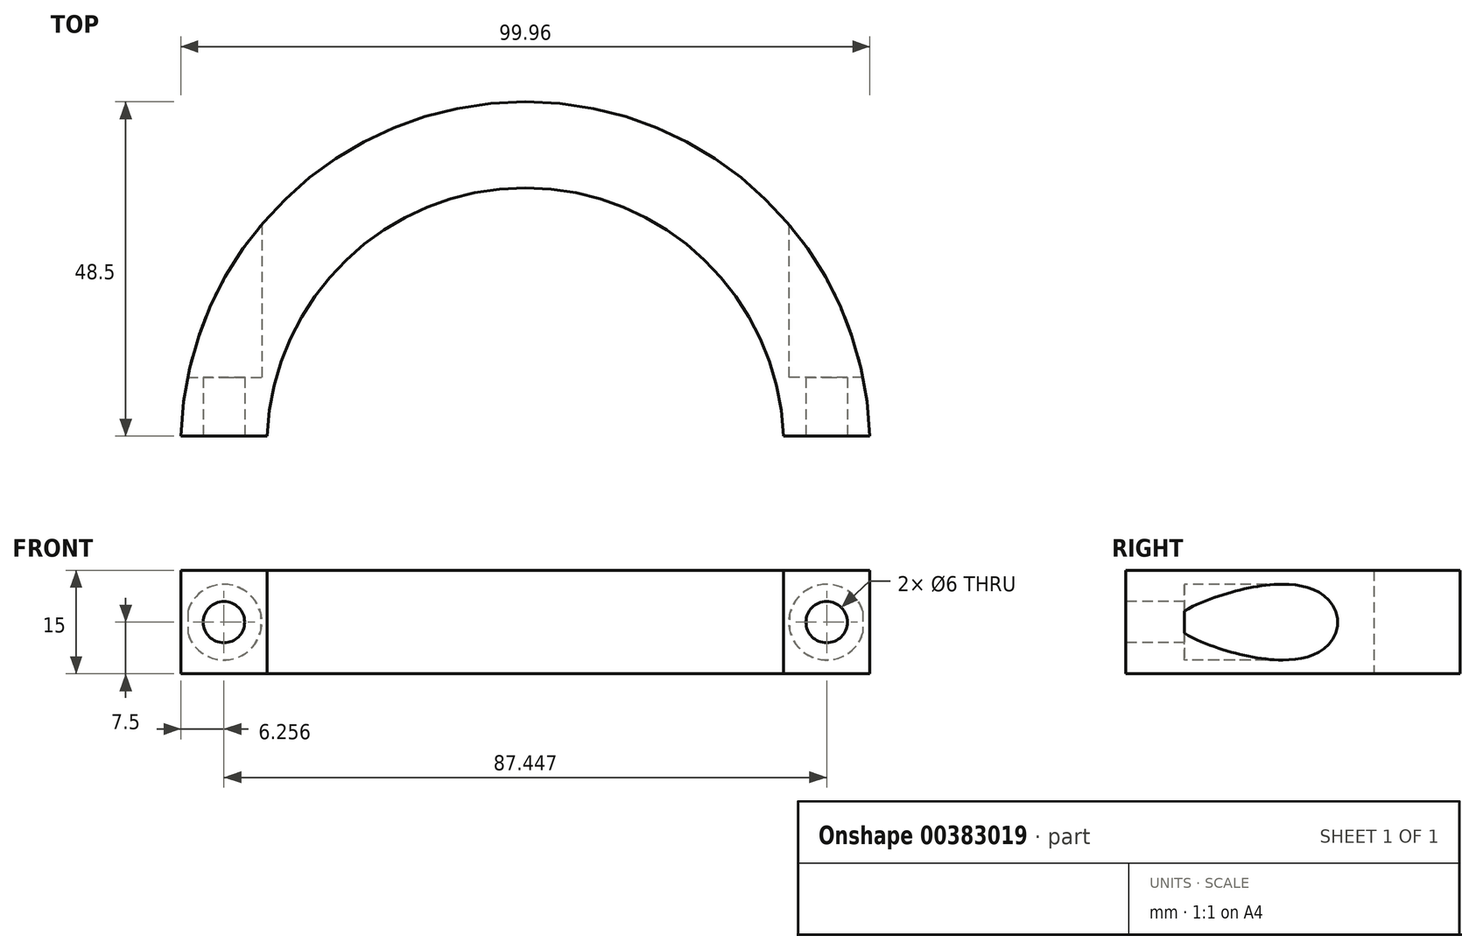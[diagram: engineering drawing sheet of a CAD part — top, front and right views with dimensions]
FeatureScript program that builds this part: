
annotation { "Feature Type Name" : "Feature", "Feature Type Description" : "" }
export const myFeature = defineFeature(function(context is Context, id is Id, definition is map)
    precondition{}
    {
        {
            var Q0;
            Q0=qCreatedBy(makeId("Top.planeOp"),FACE);
            var sketch = newSketch(context, id + "F0", { "sketchPlane" : qUnion([Q0])});
            skCircle(sketch, "E0", {"center": v(0, 0) * mm, "radius": 37.5 * mm});
            skCircle(sketch, "E1", {"center": v(0, 0) * mm, "radius": 50 * mm});
            skSolve(sketch);
        }
        {
            var Q0;
            Q0=qSketchRegion(id+"F0",true);
            extrude(context, id + "F1", {"entities" : qUnion([Q0]), "depth" : 15 * mm, "offsetDistance" : 25 * mm});
        }
        {
            var Q0;
            Q0=makeQuery(id+"F1.opExtrude","CAP_FACE",FACE,{"disambiguationData":[OSD([sQuery(id+"F0.wireOp",EDGE,"E0"),sQuery(id+"F0.wireOp",EDGE,"E1")])],"isStart":false});
            var sketch = newSketch(context, id + "F2", { "sketchPlane" : qUnion([Q0])});
            skLineSegment(sketch, "E2.bottom", {"start": v(-55, 1.5) * mm, "end": v(55, 1.5) * mm});
            skLineSegment(sketch, "E2.top", {"start": v(-55, -63.4) * mm, "end": v(55, -63.4) * mm});
            skLineSegment(sketch, "E2.left", {"start": v(-55, 1.5) * mm, "end": v(-55, -63.4) * mm});
            skLineSegment(sketch, "E2.right", {"start": v(55, 1.5) * mm, "end": v(55, -63.4) * mm});
            skSolve(sketch);
        }
        {
            var Q0;
            Q0=qSketchRegion(id+"F2",true);
            extrude(context, id + "F3", {"entities" : qUnion([Q0]), "operationType" : NewBodyOperationType.REMOVE, "endBound" : BoundingType.THROUGH_ALL, "oppositeDirection" : true, "depth" : 25 * mm, "offsetDistance" : 25 * mm});
        }
        {
            var Q0;
            Q0=qCreatedBy(makeId("Front.planeOp"),FACE);
            var sketch = newSketch(context, id + "F4", { "sketchPlane" : qUnion([Q0])});
            skLineSegment(sketch, "E3.0.0", {"start": v(-37.47, 15) * mm, "end": v(-49.98, 15) * mm, "construction": true});
            skLineSegment(sketch, "E3.0.1", {"start": v(-49.98, 15) * mm, "end": v(-49.98, 0) * mm, "construction": true});
            skLineSegment(sketch, "E3.0.2", {"start": v(-49.98, 0) * mm, "end": v(-37.47, 0) * mm, "construction": true});
            skLineSegment(sketch, "E3.0.3", {"start": v(-37.47, 0) * mm, "end": v(-37.47, 15) * mm, "construction": true});
            skLineSegment(sketch, "E4.0.0", {"start": v(37.47, 0) * mm, "end": v(49.98, 0) * mm, "construction": true});
            skLineSegment(sketch, "E4.0.1", {"start": v(49.98, 0) * mm, "end": v(49.98, 15) * mm, "construction": true});
            skLineSegment(sketch, "E4.0.2", {"start": v(49.98, 15) * mm, "end": v(37.47, 15) * mm, "construction": true});
            skLineSegment(sketch, "E4.0.3", {"start": v(37.47, 0) * mm, "end": v(37.47, 15) * mm, "construction": true});
            skLineSegment(sketch, "E5", {"start": v(-49.98, 15) * mm, "end": v(-37.47, 0) * mm, "construction": true});
            skLineSegment(sketch, "E6", {"start": v(-37.47, 15) * mm, "end": v(-49.98, 0) * mm, "construction": true});
            skLineSegment(sketch, "E7", {"start": v(37.47, 15) * mm, "end": v(49.98, 0) * mm, "construction": true});
            skLineSegment(sketch, "E8", {"start": v(49.98, 15) * mm, "end": v(37.47, 0) * mm, "construction": true});
            skCircle(sketch, "E9", {"center": v(-43.72, 7.5) * mm, "radius": 3 * mm});
            skCircle(sketch, "E10", {"center": v(43.72, 7.5) * mm, "radius": 3 * mm});
            skSolve(sketch);
        }
        {
            var Q0;
            Q0=qSketchRegion(id+"F4",true);
            extrude(context, id + "F5", {"entities" : qUnion([Q0]), "operationType" : NewBodyOperationType.REMOVE, "endBound" : BoundingType.THROUGH_ALL, "oppositeDirection" : true, "depth" : 25 * mm, "offsetDistance" : 25 * mm});
        }
        {
            var Q0;
            Q0=qCreatedBy(makeId("Front.planeOp"),FACE);
            cPlane(context, id + "F6", {"entities" : qUnion([Q0]), "cplaneType" : CPlaneType.OFFSET, "offset" : 10 * mm, "oppositeDirection" : true, "width" : 150 * mm, "height" : 150 * mm});
        }
        {
            var Q0;
            Q0=qCreatedBy(id+"F6.planeOp",FACE);
            var sketch = newSketch(context, id + "F7", { "sketchPlane" : qUnion([Q0])});
            skCircle(sketch, "E11.0", {"center": v(43.72, 7.5) * mm, "radius": 3 * mm, "construction": true});
            skCircle(sketch, "E12.0", {"center": v(-43.72, 7.5) * mm, "radius": 3 * mm, "construction": true});
            skCircle(sketch, "E13", {"center": v(43.72, 7.5) * mm, "radius": 5.5 * mm});
            skCircle(sketch, "E14", {"center": v(-43.72, 7.5) * mm, "radius": 5.5 * mm});
            skSolve(sketch);
        }
        {
            var Q0;
            Q0=qSketchRegion(id+"F7",true);
            extrude(context, id + "F8", {"entities" : qUnion([Q0]), "operationType" : NewBodyOperationType.REMOVE, "oppositeDirection" : true, "depth" : 25 * mm, "offsetDistance" : 25 * mm});
        }
    });
